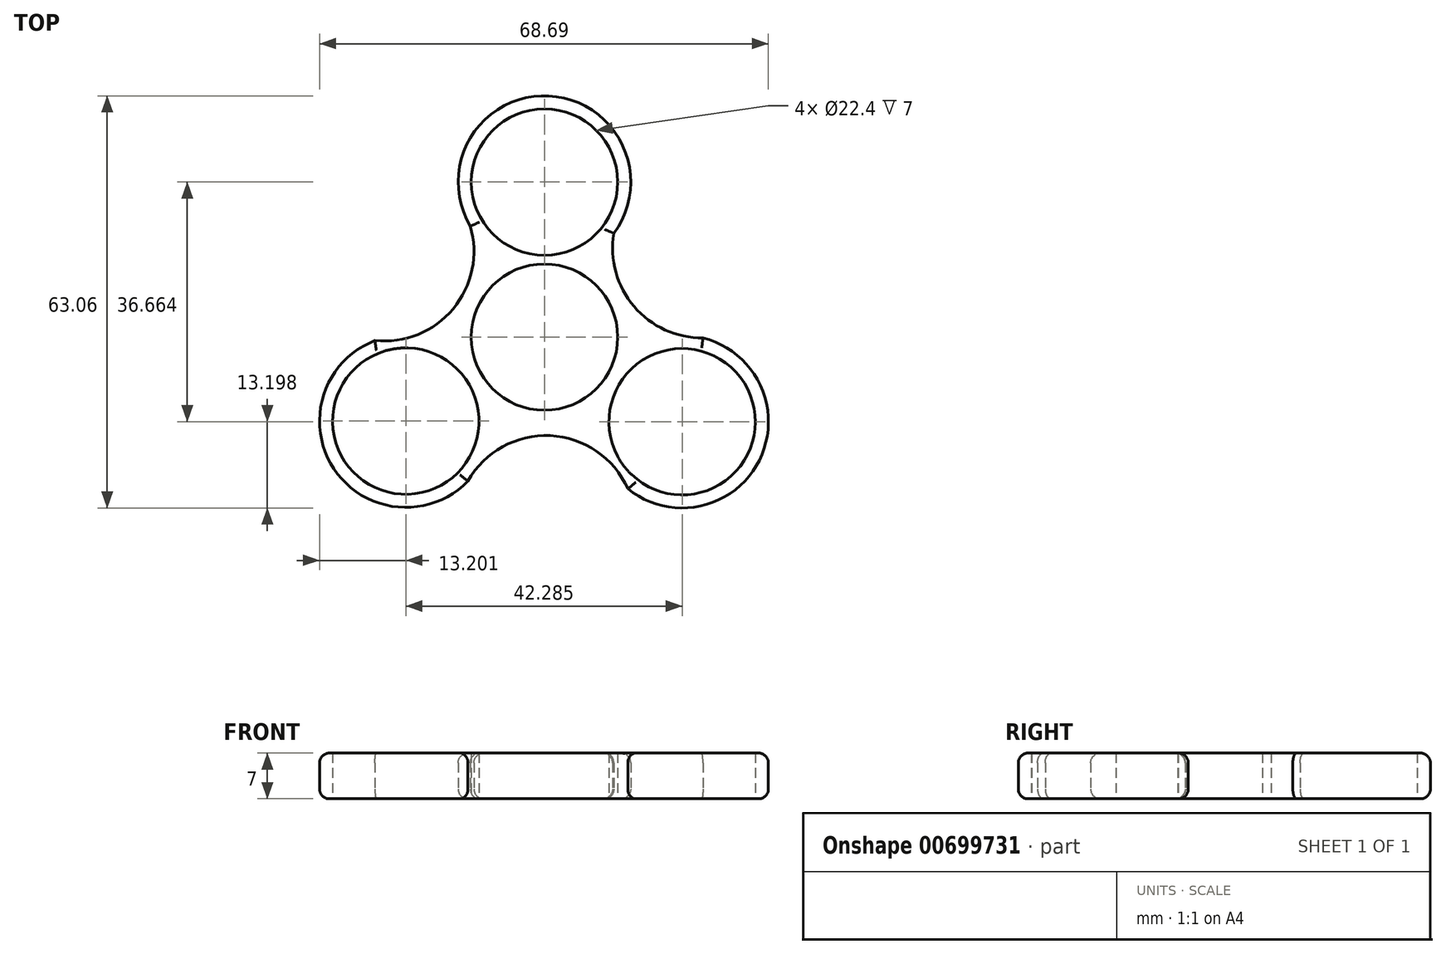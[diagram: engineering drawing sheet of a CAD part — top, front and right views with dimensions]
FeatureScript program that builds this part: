
annotation { "Feature Type Name" : "Feature", "Feature Type Description" : "" }
export const myFeature = defineFeature(function(context is Context, id is Id, definition is map)
    precondition{}
    {
        {
            var Q0;
            Q0=qCreatedBy(makeId("Top.planeOp"),FACE);
            var sketch = newSketch(context, id + "F0", { "sketchPlane" : qUnion([Q0])});
            skCircle(sketch, "E0", {"center": v(0, 0) * mm, "radius": 11.2 * mm});
            skCircle(sketch, "E1", {"center": v(0, 23.72) * mm, "radius": 11.2 * mm});
            skArc(sketch, "E2", {"start": v(10.61, 15.87) * mm, "mid": v(0.67, 36.9) * mm, "end": v(-11.35, 16.98) * mm});
            skCircle(sketch, "E3.1.0", {"center": v(-21.22, -12.85) * mm, "radius": 11.2 * mm});
            skArc(sketch, "E3.1.1", {"start": v(-19.72, 0.26) * mm, "mid": v(-33.64, -17.32) * mm, "end": v(-11.72, -22.02) * mm});
            skPoint(sketch, "E3.center", {"position": v(-0.05, -0.7) * mm});
            skCircle(sketch, "E4.1.2.0", {"center": v(21.07, -12.94) * mm, "radius": 11.2 * mm});
            skArc(sketch, "E4.2.2.0", {"start": v(12.76, -23.2) * mm, "mid": v(33.54, -17.27) * mm, "end": v(20.9, 0.26) * mm});
            skArc(sketch, "E5", {"start": v(10.61, 15.87) * mm, "mid": v(13.7, 4.69) * mm, "end": v(24.25, -0.13) * mm});
            skArc(sketch, "E6.1.0", {"start": v(-25.95, -0.53) * mm, "mid": v(-13.98, 4.33) * mm, "end": v(-11.35, 16.98) * mm});
            skArc(sketch, "E6.2.0", {"start": v(12.76, -23.2) * mm, "mid": v(0.88, -15.08) * mm, "end": v(-11.72, -22.02) * mm});
            skPoint(sketch, "E7.orphan", {"position": v(-12.69, 20.07) * mm});
            skPoint(sketch, "E8.orphan", {"position": v(13.04, 21.65) * mm});
            skSolve(sketch);
        }
        {
            var Q0;
            Q0=makeQuery(id+"F0.imprint","IMPRINT",FACE,{"disambiguationData":[TD([[makeQuery(id+"F0.imprint","IMPRINT",EDGE,{"derivedFrom":sQuery(id+"F0.wireOp",EDGE,"E0")}),-1.0]])]});
            extrude(context, id + "F1", {"entities" : qUnion([Q0]), "depth" : 7 * mm, "offsetDistance" : 25 * mm});
        }
        {
            var Q0;
            Q0=makeQuery(id+"F1.opExtrude","CAP_EDGE",EDGE,{"disambiguationData":[OSD([sQuery(id+"F0.wireOp",EDGE,"E6.2.0")])],"isStart":false});
            var Q1;
            Q1=makeQuery(id+"F1.opExtrude","CAP_EDGE",EDGE,{"disambiguationData":[OSD([sQuery(id+"F0.wireOp",EDGE,"E6.2.0")])],"isStart":true});
            var Q2;
            Q2=makeQuery(id+"F1.opExtrude","CAP_EDGE",EDGE,{"disambiguationData":[OSD([sQuery(id+"F0.wireOp",EDGE,"E3.1.1")])],"isStart":false});
            var Q3;
            Q3=makeQuery(id+"F1.opExtrude","CAP_EDGE",EDGE,{"disambiguationData":[OSD([sQuery(id+"F0.wireOp",EDGE,"E6.1.0")])],"isStart":false});
            var Q4;
            Q4=makeQuery(id+"F1.opExtrude","CAP_EDGE",EDGE,{"disambiguationData":[OSD([sQuery(id+"F0.wireOp",EDGE,"E2")])],"isStart":false});
            var Q5;
            Q5=makeQuery(id+"F1.opExtrude","CAP_EDGE",EDGE,{"disambiguationData":[OSD([sQuery(id+"F0.wireOp",EDGE,"E5")])],"isStart":false});
            var Q6;
            Q6=makeQuery(id+"F1.opExtrude","CAP_EDGE",EDGE,{"disambiguationData":[OSD([sQuery(id+"F0.wireOp",EDGE,"E4.2.2.0")])],"isStart":false});
            var Q7;
            Q7=makeQuery(id+"F1.opExtrude","CAP_EDGE",EDGE,{"disambiguationData":[OSD([sQuery(id+"F0.wireOp",EDGE,"E4.2.2.0")])],"isStart":true});
            var Q8;
            Q8=makeQuery(id+"F1.opExtrude","CAP_EDGE",EDGE,{"disambiguationData":[OSD([sQuery(id+"F0.wireOp",EDGE,"E5")])],"isStart":true});
            var Q9;
            Q9=makeQuery(id+"F1.opExtrude","CAP_EDGE",EDGE,{"disambiguationData":[OSD([sQuery(id+"F0.wireOp",EDGE,"E2")])],"isStart":true});
            var Q10;
            Q10=makeQuery(id+"F1.opExtrude","CAP_EDGE",EDGE,{"disambiguationData":[OSD([sQuery(id+"F0.wireOp",EDGE,"E3.1.1")])],"isStart":true});
            var Q11;
            Q11=makeQuery(id+"F1.opExtrude","CAP_EDGE",EDGE,{"disambiguationData":[OSD([sQuery(id+"F0.wireOp",EDGE,"E6.1.0")])],"isStart":true});
            fillet(context, id + "F2", {"entities" : qUnion([Q0, Q1, Q2, Q3, Q4, Q5, Q6, Q7, Q8, Q9, Q10, Q11]), "radius" : 1.5 * mm, "tangentPropagation" : true, "allowEdgeOverflow" : false});
        }
    });
